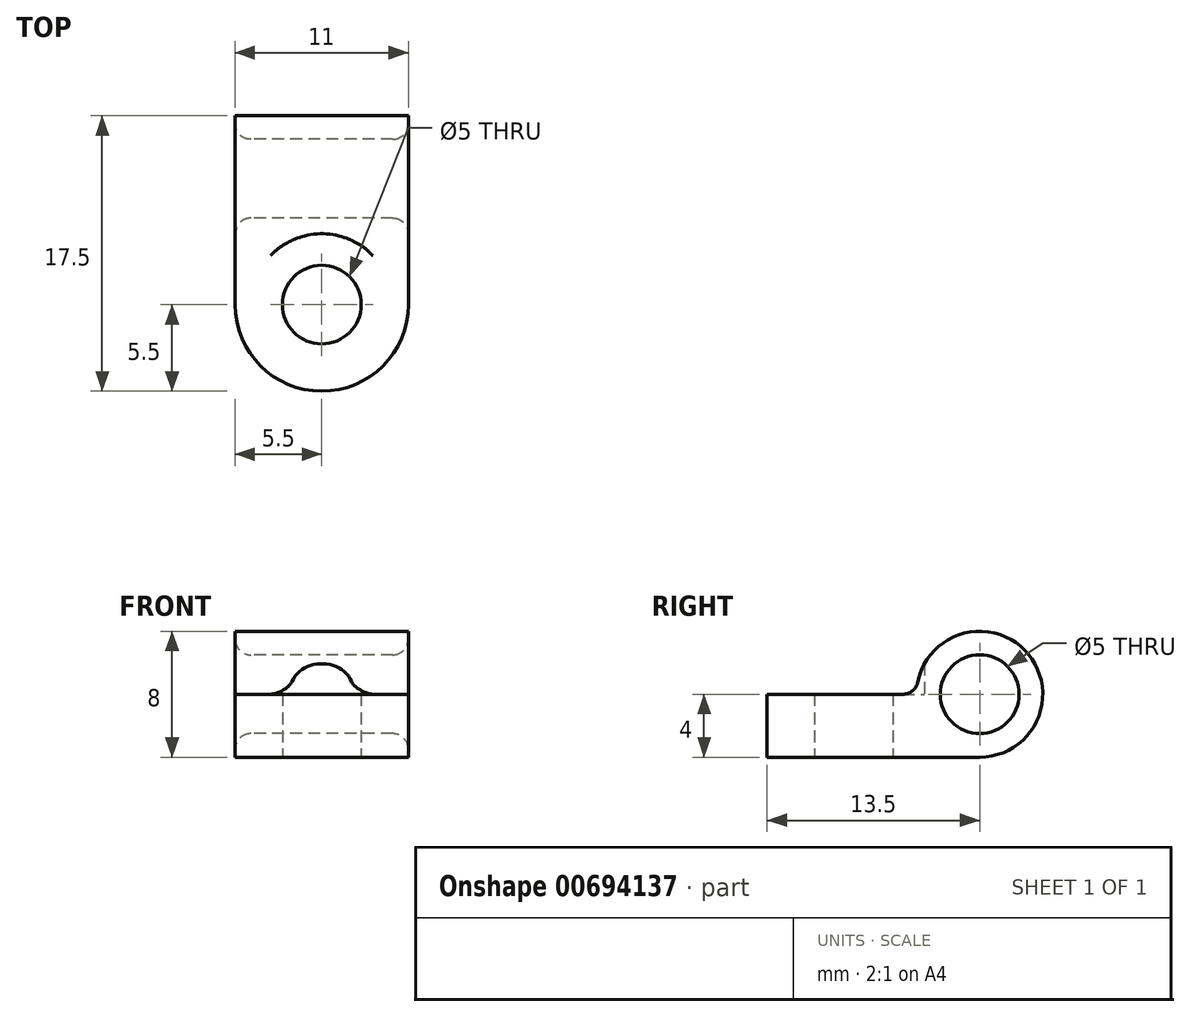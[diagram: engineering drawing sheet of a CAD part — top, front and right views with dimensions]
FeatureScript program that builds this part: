
annotation { "Feature Type Name" : "Feature", "Feature Type Description" : "" }
export const myFeature = defineFeature(function(context is Context, id is Id, definition is map)
    precondition{}
    {
        {
            var Q0;
            Q0=qCreatedBy(makeId("Top.planeOp"),FACE);
            var sketch = newSketch(context, id + "F0", { "sketchPlane" : qUnion([Q0])});
            skCircle(sketch, "E0", {"center": v(0, 0) * mm, "radius": 2.5 * mm});
            skArc(sketch, "E1", {"start": v(-5.5, 0) * mm, "mid": v(0, -5.5) * mm, "end": v(5.5, 0) * mm});
            skLineSegment(sketch, "E2", {"start": v(-5.5, 0) * mm, "end": v(-5.5, 8) * mm});
            skLineSegment(sketch, "E3", {"start": v(-5.5, 8) * mm, "end": v(5.5, 8) * mm});
            skLineSegment(sketch, "E4", {"start": v(5.5, 8) * mm, "end": v(5.5, 0) * mm});
            skSolve(sketch);
        }
        {
            var Q0;
            Q0=makeQuery(id+"F0.imprint","IMPRINT",FACE,{"disambiguationData":[TD([[makeQuery(id+"F0.imprint","IMPRINT",EDGE,{"derivedFrom":sQuery(id+"F0.wireOp",EDGE,"E0")}),-1.0]])]});
            extrude(context, id + "F1", {"entities" : qUnion([Q0]), "depth" : 4 * mm, "offsetDistance" : 25 * mm});
        }
        {
            var Q0;
            Q0=qCreatedBy(makeId("Right.planeOp"),FACE);
            var sketch = newSketch(context, id + "F2", { "sketchPlane" : qUnion([Q0])});
            skLineSegment(sketch, "E5", {"start": v(0, 0) * mm, "end": v(8, 0) * mm, "construction": true});
            skLineSegment(sketch, "E6", {"start": v(8, 0) * mm, "end": v(8, 4) * mm, "construction": true});
            skLineSegment(sketch, "E7", {"start": v(8, 4) * mm, "end": v(18.58, 4) * mm, "construction": true});
            skCircle(sketch, "E8", {"center": v(8, 4) * mm, "radius": 4 * mm});
            skCircle(sketch, "E9", {"center": v(8, 4) * mm, "radius": 2.5 * mm});
            skSolve(sketch);
        }
        {
            var Q0;
            Q0 = qSketchRegion(id + "F2", true);
            extrude(context, id + "F3", {"entities" : qUnion([Q0]), "operationType" : NewBodyOperationType.ADD, "depth" : 5.5 * mm, "offsetDistance" : 25 * mm, "hasSecondDirection" : true, "secondDirectionOppositeDirection" : true, "secondDirectionDepth" : 5.5 * mm});
        }
        {
            var Q0;
            Q0=makeQuery(id+"F2.imprint","IMPRINT",FACE,{"disambiguationData":[TD([[makeQuery(id+"F2.imprint","IMPRINT",EDGE,{"derivedFrom":sQuery(id+"F2.wireOp",EDGE,"E9")}),1.0]])]});
            extrude(context, id + "F4", {"entities" : qUnion([Q0]), "operationType" : NewBodyOperationType.REMOVE, "oppositeDirection" : true, "depth" : 25 * mm, "offsetDistance" : 25 * mm, "hasSecondDirection" : true, "secondDirectionOppositeDirection" : false, "secondDirectionDepth" : 25 * mm});
        }
        {
            var Q0;
            Q0=makeQuery(id+"F3.boolean.opBoolean","INTERSECT",EDGE,{"derivedFrom":[makeQuery(id+"F1.opExtrude","CAP_FACE",FACE,{"disambiguationData":[OSD([sQuery(id+"F0.wireOp",EDGE,"E0"),sQuery(id+"F0.wireOp",EDGE,"E1"),sQuery(id+"F0.wireOp",EDGE,"E2"),sQuery(id+"F0.wireOp",EDGE,"E3"),sQuery(id+"F0.wireOp",EDGE,"E4")])],"isStart":false}),makeQuery(id+"F3.opExtrude","SWEPT_FACE",FACE,{"disambiguationData":[OSD([sQuery(id+"F2.wireOp",EDGE,"E8")])]})]});
            fillet(context, id + "F5", {"entities" : qUnion([Q0]), "radius" : 1 * mm, "tangentPropagation" : true, "allowEdgeOverflow" : false});
        }
        {
            var Q0;
            {var subQ0=sQuery(id+"F2.wireOp",EDGE,"E9");Q0=makeQuery(id+"F4.boolean.opBoolean","INTERSECT",EDGE,{"derivedFrom":[makeQuery(id+"F3.boolean.opBoolean","MERGE",FACE,{"derivedFrom":[makeQuery(id+"F1.opExtrude","SWEPT_FACE",FACE,{"disambiguationData":[OSD([sQuery(id+"F0.wireOp",EDGE,"E4")])]}),makeQuery(id+"F3.opExtrude","CAP_FACE",FACE,{"disambiguationData":[OSD([sQuery(id+"F2.wireOp",EDGE,"E8"),subQ0])],"isStart":false})]}),makeQuery(id+"F4.opExtrude","SWEPT_FACE",FACE,{"disambiguationData":[OSD([subQ0])]})]});}
            var Q1;
            {var subQ0=sQuery(id+"F2.wireOp",EDGE,"E9");Q1=makeQuery(id+"F4.boolean.opBoolean","INTERSECT",EDGE,{"derivedFrom":[makeQuery(id+"F3.boolean.opBoolean","MERGE",FACE,{"derivedFrom":[makeQuery(id+"F1.opExtrude","SWEPT_FACE",FACE,{"disambiguationData":[OSD([sQuery(id+"F0.wireOp",EDGE,"E2")])]}),makeQuery(id+"F3.opExtrude","CAP_FACE",FACE,{"disambiguationData":[OSD([sQuery(id+"F2.wireOp",EDGE,"E8"),subQ0])],"isStart":true})]}),makeQuery(id+"F4.opExtrude","SWEPT_FACE",FACE,{"disambiguationData":[OSD([subQ0])]})]});}
            fillet(context, id + "F6", {"entities" : qUnion([Q0, Q1]), "radius" : 1 * mm, "tangentPropagation" : true, "allowEdgeOverflow" : false});
        }
        {
            var Q0;
            Q0=qCreatedBy(makeId("Top.planeOp"),FACE);
            var sketch = newSketch(context, id + "F7", { "sketchPlane" : qUnion([Q0])});
            skCircle(sketch, "E10", {"center": v(0, 0) * mm, "radius": 4.5 * mm});
            skSolve(sketch);
        }
        {
            var Q0;
            Q0 = qSketchRegion(id + "F7", true);
            extrude(context, id + "F8", {"entities" : qUnion([Q0]), "operationType" : NewBodyOperationType.REMOVE, "depth" : 25 * mm, "offsetDistance" : 25 * mm, "hasSecondDirection" : true, "secondDirectionOppositeDirection" : false, "secondDirectionDepth" : 4 * mm});
        }
    });
